# Revit family: Lighting_Pendants_Zero_Daikanyama_Pendant
name_source: partatom
category: Lighting Fixtures
units: mm (PartAtom-declared; Revit-internal decimal feet)

## family parameters
Always vertical = Yes
Cut with Voids When Loaded = No
Light Source = Yes
OmniClass Number = 23.80.70.00
OmniClass Title = Lighting
Part Type = Normal
Room Calculation Point = No
Round Connector Dimension = Use Diameter
Shared = No
Work Plane-Based = Yes

## types (2) — shared parameters
AssetType = Fixed
BIMObjectName = Lighting_Pendants_Zero_Daikanyama_Pendant
Brand = Zero
Brand url = http://www.zero.se
Category = Pendant
Collection = Daikanyama
Color = Black, orange, red, white or yellow
Color Filter = 16777215
Design country = Sweden
Designer = Thomas Bernstrand
Dimming Lamp Color Temperature Shift = <None>
DurationUnit = Year
Edition number = 1
Features = Terminal block 3x2,25mm2
Finish = Painted aluminum and opal glass
HasProtectiveEarth = No
IP_Code = IP20
IfcExportAs = IfcLightFixtureType
IfcExportType = NOTDEFINED
LensMaterial = Glass, Frosted
LightFixtureMountingType = Suspended
LightFixturePlacingType = Ceiling
Manufacturer = Zero
Manufacturer country = Sweden
Manufacturer name = ZERO
ManufacturerName = Zero
ManufacturerURL = https://www.zerolighting.com
Material = Metal and glass
Material main = Aluminium
Material secondary = Glass
NBSDescription = General purpose luminaires
NBSReference = 90-60-50/405
Name = Zero_Daikanyama_Pendant
Nominal height = 285 mm  [stored 0.935039 ft]
Nominal width = 420 mm  [stored 1.37795 ft]
NominalCurrent = 0 A
NominalDiameter = 420 mm  [stored 1.37795 ft]
NominalFrequencyRange = 50 Hz
NominalLength = 420 mm  [stored 1.37795 ft]
NominalRadius = 210 mm  [stored 0.688976 ft]
NominalVoltage = 230 V
NominalVoltageCalc = 0 V
Note = Article numbers change according shade colors.XX = -01 White, -06 Black, -07 Red, -14 Yellow, -41 Orange.
NumberOfPoles = 1
PhaseAngle = 0.00°
Photometric Web File = Daikanyama8265_IES.IES
Product Guid = 0f3bce4b-4a32-47e0-8b4d-7e71d0f050cd
Product SKU = Daikanyama_pendant
Product family = Daikanyama
Product group = Pendant
Revision = 5
Shape = Cylinder
Size = 420x420x285 mm
URL = https://www.zerolighting.com
Uniclass2 = Pr_70_70_49_86
Uniclass2015Description = Suspended luminaires
Uniclass2015Reference = Pr_70_70_48_86
UsageCurrent = 0 A
Version = 3
VersionDate = 31/08/2023
WarrantyDurationUnit = Year
Weight Net (Kg) = 1.8
zero-valued in all types: ElectricalDeviceNominalPower, MaintenanceFactor, NumberOfSources

## per-type parameters (varying)
| type | ArticleNumber | Model | ModelNumber | Tilt Angle | TotalWattage |
| Daikanyama pendant LED 10W/E27 | 8267-1-XX | Daikanyama pendant  LED 10W/E27 | 8267-1-XX | 90.00° | 10 W |
| Daikanyama pendant Max 42W/E27 | 8259-1-XX | Daikanyama pendant Max 42W/E27 | 8259-1-XX | 60.00° | 42 W |

note: [stored X ft] marks values corroborated as IEEE doubles in the binary element streams (Revit-internal decimal feet)

## geometry (parser evidence)
native form markers: Sweep x7
no freeform markers — native parametric forms only
